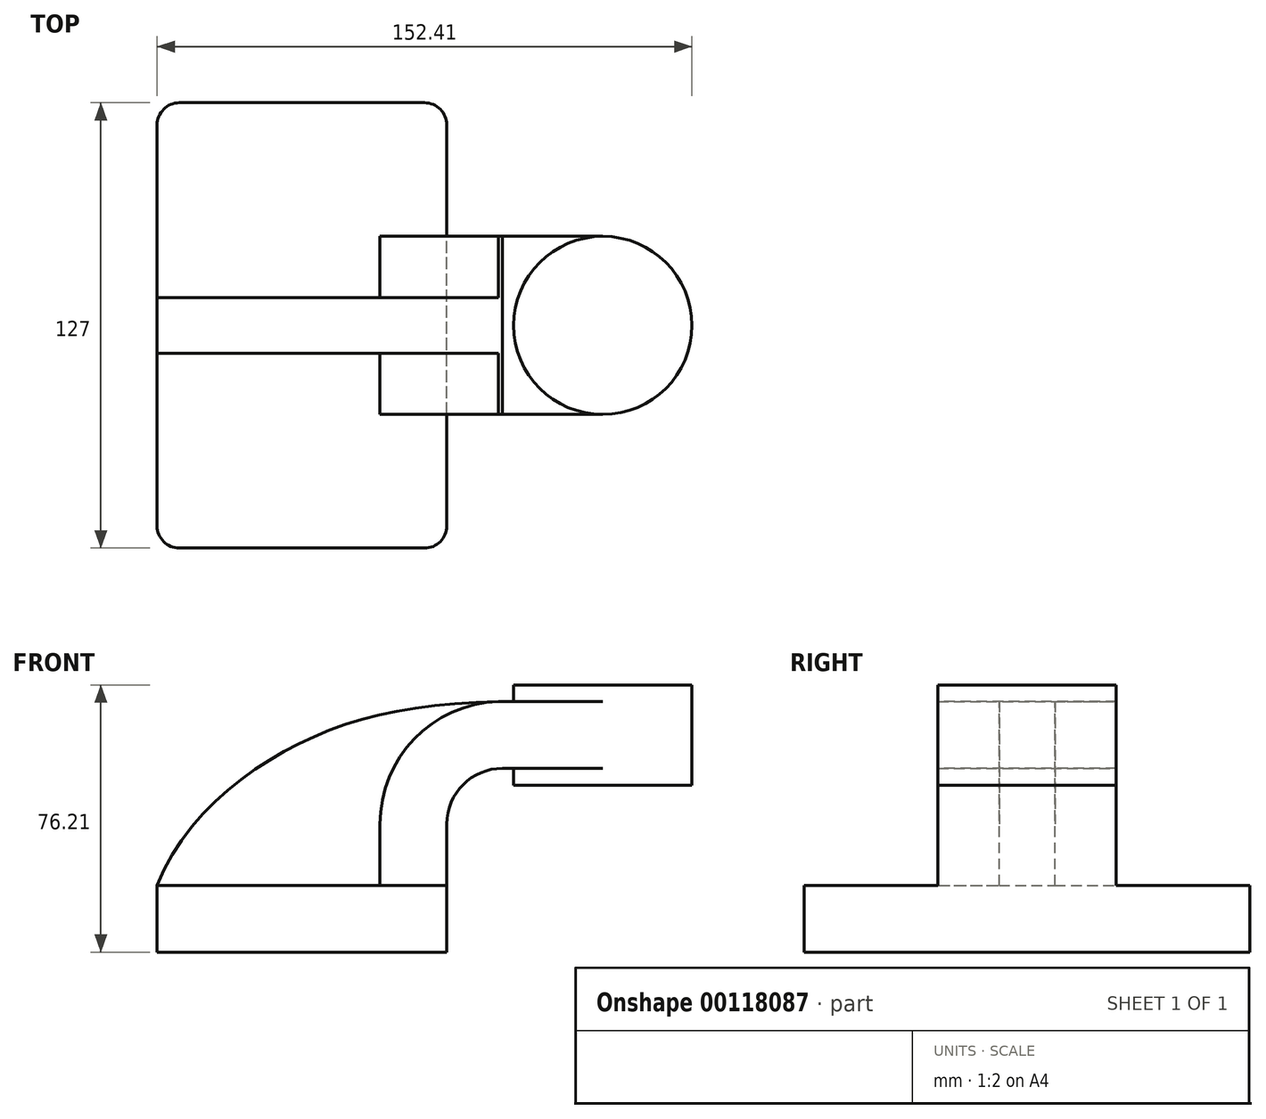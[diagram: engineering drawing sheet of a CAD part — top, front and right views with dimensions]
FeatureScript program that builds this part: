
annotation { "Feature Type Name" : "Feature", "Feature Type Description" : "" }
export const myFeature = defineFeature(function(context is Context, id is Id, definition is map)
    precondition{}
    {
        {
            var Q0;
            Q0=qCreatedBy(makeId("Front.planeOp"),FACE);
            var sketch = newSketch(context, id + "F0", { "sketchPlane" : qUnion([Q0])});
            skLineSegment(sketch, "E0.bottom", {"start": v(41.28, -9.52) * mm, "end": v(-41.28, -9.53) * mm});
            skLineSegment(sketch, "E0.top", {"start": v(41.28, 9.53) * mm, "end": v(-41.28, 9.53) * mm});
            skLineSegment(sketch, "E0.left", {"start": v(41.28, -9.52) * mm, "end": v(41.28, 9.53) * mm});
            skLineSegment(sketch, "E0.right", {"start": v(-41.28, -9.53) * mm, "end": v(-41.28, 9.53) * mm});
            skPoint(sketch, "E0.middle", {"position": v(0, 0) * mm});
            skLineSegment(sketch, "E1.bottom", {"start": v(111.13, 38.1) * mm, "end": v(60.33, 38.1) * mm});
            skLineSegment(sketch, "E1.top", {"start": v(111.13, 66.68) * mm, "end": v(60.33, 66.68) * mm});
            skLineSegment(sketch, "E1.left", {"start": v(111.13, 38.1) * mm, "end": v(111.13, 66.68) * mm});
            skLineSegment(sketch, "E1.right", {"start": v(60.33, 38.1) * mm, "end": v(60.33, 66.68) * mm});
            skPoint(sketch, "E1.middle", {"position": v(85.73, 52.39) * mm});
            skLineSegment(sketch, "E2", {"start": v(41.28, 9.53) * mm, "end": v(41.28, 27) * mm});
            skArc(sketch, "E3", {"start": v(41.27, 27) * mm, "mid": v(45.92, 38.23) * mm, "end": v(57.15, 42.88) * mm});
            skLineSegment(sketch, "E4", {"start": v(57.15, 42.88) * mm, "end": v(85.73, 42.88) * mm});
            skLineSegment(sketch, "E5.0", {"start": v(57.15, 61.93) * mm, "end": v(85.73, 61.93) * mm});
            skArc(sketch, "E5.1", {"start": v(22.23, 27) * mm, "mid": v(32.45, 51.7) * mm, "end": v(57.15, 61.93) * mm});
            skLineSegment(sketch, "E5.2", {"start": v(22.23, 9.53) * mm, "end": v(22.23, 27) * mm});
            skLineSegment(sketch, "E6", {"start": v(85.73, 66.68) * mm, "end": v(85.73, 38.1) * mm});
            skFitSpline(sketch, "E7", {"points": [v(-41.28, 9.53) * mm, v(-4.88, 47.78) * mm, v(57.15, 61.93) * mm], "startDerivative": vector(41.4, 106.14) * mm, "endDerivative": vector(151.57, 2.32) * mm});
            skSolve(sketch);
        }
        {
            var Q0;
            Q0=makeQuery(id+"F0.imprint","IMPRINT",FACE,{"disambiguationData":[TD([[makeQuery(id+"F0.imprint","IMPRINT",EDGE,{"derivedFrom":sQuery(id+"F0.wireOp",EDGE,"E0.bottom")}),-1.0]])]});
            extrude(context, id + "F1", {"entities" : qUnion([Q0]), "endBound" : BoundingType.SYMMETRIC, "depth" : 127 * mm});
        }
        {
            var Q0;
            {var subQ1=sQuery(id+"F0.wireOp",EDGE,"E2");Q0=makeQuery(id+"F0.imprint","IMPRINT",FACE,{"disambiguationData":[TD([[makeQuery(id+"F0.imprint","IMPRINT",EDGE,{"derivedFrom":subQ1}),1.0]])]});}
            var Q1;
            {var subQ0=sQuery(id+"F0.wireOp",EDGE,"E4");var subQ1=sQuery(id+"F0.wireOp",EDGE,"E1.right");var subQ2=makeQuery(id+"F0.imprint","INTERSECT",VERTEX,{"derivedFrom":[subQ1,subQ0]});Q1=makeQuery(id+"F0.imprint","IMPRINT",FACE,{"disambiguationData":[TD([[makeQuery(id+"F0.imprint","IMPRINT",EDGE,{"disambiguationData":[TD([[subQ2,-1.0]])],"derivedFrom":subQ1}),-1.0]])]});}
            extrude(context, id + "F2", {"entities" : qUnion([Q0, Q1]), "operationType" : NewBodyOperationType.ADD, "endBound" : BoundingType.SYMMETRIC, "depth" : 50.8 * mm});
        }
        {
            var Q0;
            {var subQ3=sQuery(id+"F0.wireOp",EDGE,"E5.2");Q0=makeQuery(id+"F0.imprint","IMPRINT",FACE,{"disambiguationData":[TD([[makeQuery(id+"F0.imprint","IMPRINT",EDGE,{"derivedFrom":subQ3}),1.0]])]});}
            extrude(context, id + "F3", {"entities" : qUnion([Q0]), "operationType" : NewBodyOperationType.ADD, "endBound" : BoundingType.SYMMETRIC, "depth" : 15.88 * mm});
        }
        {
            var Q0;
            {var subQ0=sQuery(id+"F0.wireOp",EDGE,"E1.left");Q0=makeQuery(id+"F0.imprint","IMPRINT",FACE,{"disambiguationData":[TD([[makeQuery(id+"F0.imprint","IMPRINT",EDGE,{"derivedFrom":subQ0}),1.0]])]});}
            var Q1;
            Q1=sQuery(id+"F0.wireOp",EDGE,"E6");
            revolve(context, id + "F4", {"operationType" : NewBodyOperationType.ADD, "entities" : qUnion([Q0]), "axis" : qUnion([Q1]), "revolveType" : RevolveType.FULL});
        }
        {
            var Q0;
            Q0=makeQuery(id+"F1.opExtrude","CAP_EDGE",EDGE,{"disambiguationData":[OSD([sQuery(id+"F0.wireOp",EDGE,"E0.right")])],"isStart":false});
            var Q1;
            Q1=makeQuery(id+"F1.opExtrude","CAP_EDGE",EDGE,{"disambiguationData":[OSD([sQuery(id+"F0.wireOp",EDGE,"E0.left")])],"isStart":false});
            var Q2;
            Q2=makeQuery(id+"F1.opExtrude","CAP_EDGE",EDGE,{"disambiguationData":[OSD([sQuery(id+"F0.wireOp",EDGE,"E0.left")])],"isStart":true});
            var Q3;
            Q3=makeQuery(id+"F1.opExtrude","CAP_EDGE",EDGE,{"disambiguationData":[OSD([sQuery(id+"F0.wireOp",EDGE,"E0.right")])],"isStart":true});
            fillet(context, id + "F5", {"entities" : qUnion([Q0, Q1, Q2, Q3]), "radius" : 6.35 * mm, "tangentPropagation" : true, "allowEdgeOverflow" : false});
        }
    });
